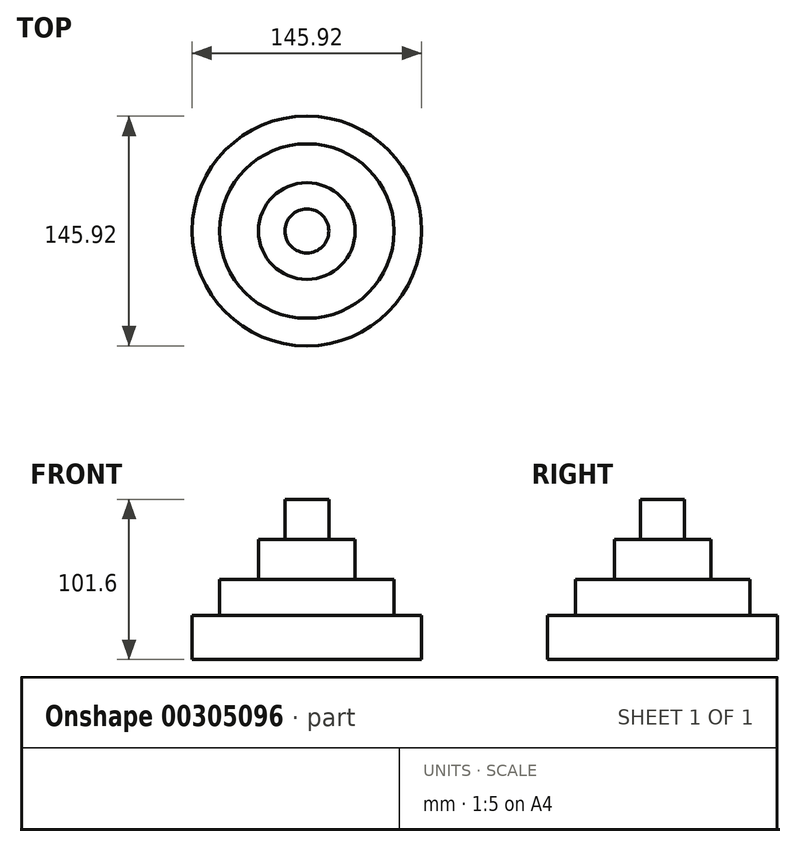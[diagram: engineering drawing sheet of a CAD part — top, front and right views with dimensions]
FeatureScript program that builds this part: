
annotation { "Feature Type Name" : "Feature", "Feature Type Description" : "" }
export const myFeature = defineFeature(function(context is Context, id is Id, definition is map)
    precondition{}
    {
        {
            var Q0;
            Q0=qCreatedBy(makeId("Top.planeOp"),FACE);
            var sketch = newSketch(context, id + "F0", { "sketchPlane" : qUnion([Q0])});
            skCircle(sketch, "E0", {"center": v(0, 0) * mm, "radius": 72.96 * mm});
            skSolve(sketch);
        }
        {
            var Q0;
            Q0=qCreatedBy(makeId("Top.planeOp"),FACE);
            var sketch = newSketch(context, id + "F1", { "sketchPlane" : qUnion([Q0])});
            skCircle(sketch, "E1", {"center": v(0, 0) * mm, "radius": 55.4 * mm});
            skSolve(sketch);
        }
        {
            var Q0;
            Q0 = qSketchRegion(id + "F1", true);
            extrude(context, id + "F2", {"entities" : qUnion([Q0]), "depth" : 25.4 * mm});
        }
        {
            var Q0;
            Q0=qCreatedBy(makeId("Top.planeOp"),FACE);
            var sketch = newSketch(context, id + "F3", { "sketchPlane" : qUnion([Q0])});
            skText(sketch, "E2", { "text": "PEACE\n", "fontName": "OpenSans-BoldItalic.ttf"});
            const initialGuessF3  = {"E2": [-0.03478, 0, 1, 0, 0.01801]};
            skSetInitialGuess(sketch, initialGuessF3);
            skSolve(sketch);
        }
        {
            var Q0;
            Q0 = qSketchRegion(id + "F3", true);
            extrude(context, id + "F4", {"entities" : qUnion([Q0]), "operationType" : NewBodyOperationType.ADD, "depth" : 25.4 * mm});
        }
        {
            var Q0;
            Q0=qCreatedBy(makeId("Top.planeOp"),FACE);
            var sketch = newSketch(context, id + "F5", { "sketchPlane" : qUnion([Q0])});
            skSolve(sketch);
        }
        {
            var Q0;
            Q0 = qSketchRegion(id + "F5", true);
            var Q1;
            Q1=makeQuery(id+"F2.opExtrude","CAP_FACE",FACE,{"disambiguationData":[OSD([sQuery(id+"F1.wireOp",EDGE,"E1")])],"isStart":false});
            extrude(context, id + "F6", {"entities" : qUnion([Q0, Q1]), "operationType" : NewBodyOperationType.ADD, "depth" : 25.4 * mm});
        }
        {
            var Q0;
            Q0=makeQuery(id+"F0.imprint","IMPRINT",FACE,{"disambiguationData":[TD([[makeQuery(id+"F0.imprint","IMPRINT",EDGE,{"derivedFrom":sQuery(id+"F0.wireOp",EDGE,"E0")}),1.0]])]});
            extrude(context, id + "F7", {"entities" : qUnion([Q0]), "operationType" : NewBodyOperationType.ADD, "depth" : 27.94 * mm});
        }
        {
            var Q0;
            Q0=makeQuery(id+"F6.opExtrude","CAP_FACE",FACE,{"disambiguationData":[OSD([sQuery(id+"F1.wireOp",EDGE,"E1")])],"isStart":false});
            var sketch = newSketch(context, id + "F8", { "sketchPlane" : qUnion([Q0])});
            skCircle(sketch, "E3", {"center": v(0, 0) * mm, "radius": 30.72 * mm});
            skSolve(sketch);
        }
        {
            var Q0;
            Q0 = qSketchRegion(id + "F8", true);
            extrude(context, id + "F9", {"entities" : qUnion([Q0]), "operationType" : NewBodyOperationType.ADD, "depth" : 25.4 * mm});
        }
        {
            var Q0;
            Q0=makeQuery(id+"F9.opExtrude","CAP_FACE",FACE,{"disambiguationData":[OSD([sQuery(id+"F8.wireOp",EDGE,"E3")])],"isStart":false});
            var sketch = newSketch(context, id + "F10", { "sketchPlane" : qUnion([Q0])});
            skCircle(sketch, "E4", {"center": v(0, 0) * mm, "radius": 13.97 * mm});
            skSolve(sketch);
        }
        {
            var Q0;
            Q0 = qSketchRegion(id + "F10", true);
            extrude(context, id + "F11", {"entities" : qUnion([Q0]), "operationType" : NewBodyOperationType.ADD, "depth" : 25.4 * mm});
        }
    });
